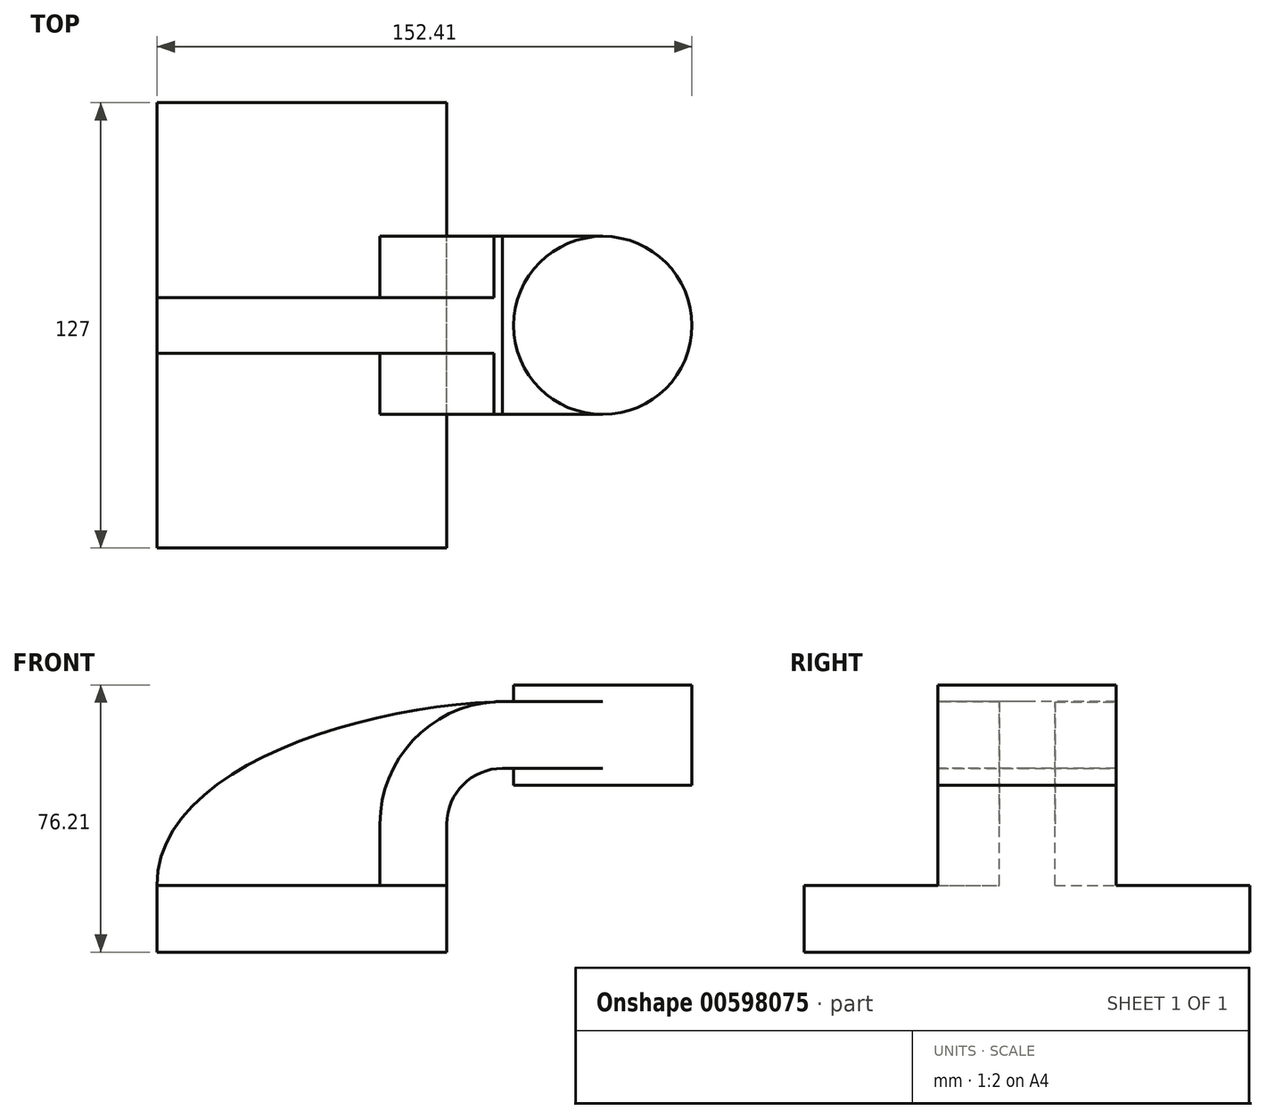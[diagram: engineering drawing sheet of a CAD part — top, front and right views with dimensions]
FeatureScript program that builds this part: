
annotation { "Feature Type Name" : "Feature", "Feature Type Description" : "" }
export const myFeature = defineFeature(function(context is Context, id is Id, definition is map)
    precondition{}
    {
        {
            var Q0;
            Q0=qCreatedBy(makeId("Front.planeOp"),FACE);
            var sketch = newSketch(context, id + "F0", { "sketchPlane" : qUnion([Q0])});
            skLineSegment(sketch, "E0.bottom", {"start": v(41.27, 9.53) * mm, "end": v(-41.28, 9.53) * mm});
            skLineSegment(sketch, "E0.top", {"start": v(41.28, -9.52) * mm, "end": v(-41.27, -9.52) * mm});
            skLineSegment(sketch, "E0.left", {"start": v(41.28, 9.53) * mm, "end": v(41.28, -9.52) * mm});
            skLineSegment(sketch, "E0.right", {"start": v(-41.28, 9.53) * mm, "end": v(-41.27, -9.52) * mm});
            skPoint(sketch, "E0.middle", {"position": v(0, 0) * mm});
            skLineSegment(sketch, "E1.bottom", {"start": v(111.13, 38.1) * mm, "end": v(60.33, 38.1) * mm});
            skLineSegment(sketch, "E1.top", {"start": v(111.13, 66.68) * mm, "end": v(60.33, 66.68) * mm});
            skLineSegment(sketch, "E1.left", {"start": v(111.13, 38.1) * mm, "end": v(111.13, 66.68) * mm});
            skLineSegment(sketch, "E1.right", {"start": v(60.33, 38.1) * mm, "end": v(60.33, 66.68) * mm});
            skPoint(sketch, "E1.middle", {"position": v(85.73, 52.39) * mm});
            skLineSegment(sketch, "E2", {"start": v(41.27, 9.53) * mm, "end": v(41.27, 27) * mm});
            skArc(sketch, "E3", {"start": v(41.27, 27) * mm, "mid": v(45.92, 38.23) * mm, "end": v(57.15, 42.88) * mm});
            skLineSegment(sketch, "E4", {"start": v(57.15, 42.88) * mm, "end": v(85.73, 42.88) * mm});
            skLineSegment(sketch, "E5.0", {"start": v(57.15, 61.93) * mm, "end": v(85.73, 61.93) * mm});
            skArc(sketch, "E5.1", {"start": v(22.22, 27) * mm, "mid": v(32.45, 51.7) * mm, "end": v(57.15, 61.93) * mm});
            skLineSegment(sketch, "E5.2", {"start": v(22.22, 9.53) * mm, "end": v(22.22, 27) * mm});
            skLineSegment(sketch, "E6", {"start": v(85.73, 38.1) * mm, "end": v(85.73, 66.68) * mm});
            skFitSpline(sketch, "E7", {"points": [v(-41.28, 9.52) * mm, v(57.15, 61.93) * mm], "startDerivative": vector(-0.96, 100.44) * mm, "endDerivative": vector(120.79, 3.21) * mm});
            skSolve(sketch);
        }
        {
            var Q0;
            Q0=makeQuery(id+"F0.imprint","IMPRINT",FACE,{"disambiguationData":[TD([[makeQuery(id+"F0.imprint","IMPRINT",EDGE,{"derivedFrom":sQuery(id+"F0.wireOp",EDGE,"E0.top")}),-1.0]])]});
            extrude(context, id + "F1", {"entities" : qUnion([Q0]), "endBound" : BoundingType.SYMMETRIC, "depth" : 127 * mm, "offsetDistance" : 25.4 * mm});
        }
        {
            var Q0;
            {var subQ0=sQuery(id+"F0.wireOp",EDGE,"E4");var subQ1=sQuery(id+"F0.wireOp",EDGE,"E1.right");var subQ2=makeQuery(id+"F0.imprint","INTERSECT",VERTEX,{"derivedFrom":[subQ1,subQ0]});Q0=makeQuery(id+"F0.imprint","IMPRINT",FACE,{"disambiguationData":[TD([[makeQuery(id+"F0.imprint","IMPRINT",EDGE,{"disambiguationData":[TD([[subQ2,-1.0]])],"derivedFrom":subQ1}),-1.0]])]});}
            var Q1;
            {var subQ1=sQuery(id+"F0.wireOp",EDGE,"E2");Q1=makeQuery(id+"F0.imprint","IMPRINT",FACE,{"disambiguationData":[TD([[makeQuery(id+"F0.imprint","IMPRINT",EDGE,{"derivedFrom":subQ1}),1.0]])]});}
            extrude(context, id + "F2", {"entities" : qUnion([Q0, Q1]), "operationType" : NewBodyOperationType.ADD, "endBound" : BoundingType.SYMMETRIC, "depth" : 50.8 * mm, "offsetDistance" : 25.4 * mm});
        }
        {
            var Q0;
            {var subQ3=sQuery(id+"F0.wireOp",EDGE,"E5.2");Q0=makeQuery(id+"F0.imprint","IMPRINT",FACE,{"disambiguationData":[TD([[makeQuery(id+"F0.imprint","IMPRINT",EDGE,{"derivedFrom":subQ3}),1.0]])]});}
            extrude(context, id + "F3", {"entities" : qUnion([Q0]), "operationType" : NewBodyOperationType.ADD, "endBound" : BoundingType.SYMMETRIC, "depth" : 15.88 * mm, "offsetDistance" : 25.4 * mm});
        }
        {
            var Q0;
            {var subQ0=sQuery(id+"F0.wireOp",EDGE,"E1.left");Q0=makeQuery(id+"F0.imprint","IMPRINT",FACE,{"disambiguationData":[TD([[makeQuery(id+"F0.imprint","IMPRINT",EDGE,{"derivedFrom":subQ0}),1.0]])]});}
            var Q1;
            Q1=sQuery(id+"F0.wireOp",EDGE,"E6");
            revolve(context, id + "F4", {"operationType" : NewBodyOperationType.ADD, "entities" : qUnion([Q0]), "axis" : qUnion([Q1]), "revolveType" : RevolveType.FULL});
        }
    });
